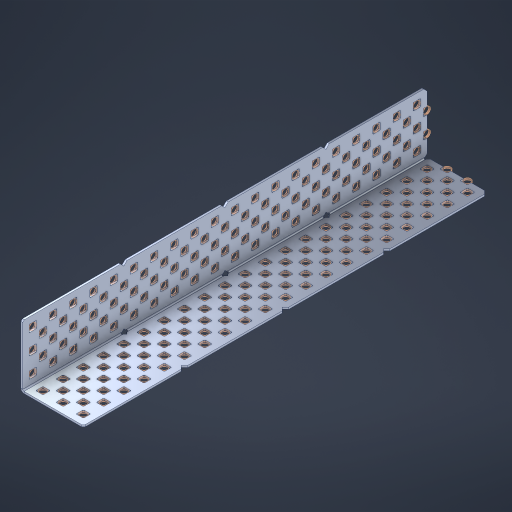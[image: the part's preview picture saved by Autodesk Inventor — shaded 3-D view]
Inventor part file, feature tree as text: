
AUTODESK INVENTOR PART (.ipt)
format: ipt  version: 2023 (Build 270158000, 158)  size: 2,148,352 bytes
history: native  units: in
note: dims shown in document units (in); Inventor stores cm internally (conversion verified against a paired STEP export)
features: other x206, extrude x198, sheet_metal_op x8, sketch x7, pattern_linear x3, mirror x1, chamfer x1
ambient origin geometry x8: Origin, YZ Plane, XZ Plane, XY Plane, X Axis, Y Axis, Z Axis, Center Point
bodies: Solid1 (feature_tree), Body (feature_tree)
feature tree (424):
  sheet_metal_op  "Flanges"
  sheet_metal_op  "Body Pattern"
  pattern_linear  "Center Double"  Spacing1=1.5in  [1 undecoded]
  pattern_linear  "Center Pattern"  Spacing1=0.1875in  [1 undecoded]
  other  "Arc Length"
  pattern_linear  "Notch Pattern"  Spacing1=0.0469in  [1 undecoded]
  other  "Diagonal Plane"
  mirror  "Everything Mirrored"
  chamfer  "End Chamfer"
  sketch  "Sketch1"  dims[d0=1.5in]
  other  "Plate1"
  sketch  "Sketch2"  dims[d1=10.0in]
  other  "Plate2"
  sheet_metal_op  "Bend1"
  sheet_metal_op  "Corner1"
  sketch  "Sketch8"  dims[d2=0.0469in]
  sketch  "Sketch9"  dims[d3=0.0469in]
  other  "Srf91"
  sheet_metal_op  "Body Pattern Sketch"
  other  "Srf92"
  sketch  "Sketch13"  dims[d4=0.0234in]
  sketch  "Sketch15"  dims[d5=0.0938in]
  sketch  "Sketch16"  dims[d6=0.0469in d7=1.5in d8=90.0deg d9=0.0312in d10=0.1875in d11=0.0469in d12=0.0469in d49=0.182in d50=0.02in d52=0.25in d53=0.0469in d54=0.0in d55=0.172in d56=1.0in d57=0.0in d85=0.1473in d86=0.1659in d89=0.0469in d90=0.0in d91=0.04in d92=0.0491in d95=2.5in d96=0.04in d97=0.25in d98=45.0deg d106=0.182in d107=0.02in d110=0.0469in d111=0.0in d112=0.172in d113=0.5in d114=0.0in d117=0.5in d126=0.0491in d127=0.1227in d128=0.08in d129=0.04in d130=2.5in d131=0.25in d132=7.874in d134=0.5in d135=1.1811in d137=0.5in d140=0.5in d141=1.0in d142=0.3937in d144=0.5in d145=0.071in d146=0.7874in d148=0.5in]
  other  "Srf786"
  other  "Srf856"
  other  "Srf889"
  other  "Srf890"
  other  "Srf891"
  other  "Srf1275"
  other  "Srf1276"
  other  "Srf1278"
  other  "Srf1277"
  other  "Srf1285"
  other  "Srf1286"
  other  "Srf1287"
  other  "Srf1445"
  other  "Srf1446"
  other  "Srf1447"
  other  "Srf1448"
  other  "Srf1449"
  other  "Srf1537"
  other  "Srf1538"
  other  "Srf1539"
  other  "Srf1540"
  other  "Srf1541"
  other  "Srf1807"
  other  "Srf1808"
  other  "Srf1809"
  other  "Srf1810"
  other  "Srf1811"
  other  "Srf1812"
  other  "Srf1813"
  other  "Srf1814"
  other  "Srf1815"
  other  "Srf1816"
  other  "Srf1817"
  other  "Srf1959"
  other  "Srf1960"
  other  "Srf1961"
  other  "Srf1962"
  other  "Srf1963"
  other  "Srf1964"
  other  "Srf1965"
  other  "Srf1966"
  other  "Srf1967"
  other  "Srf1968"
  other  "Srf1969"
  other  "Srf2009"
  other  "Srf2010"
  other  "Srf2011"
  other  "Srf2012"
  other  "Srf2013"
  other  "Srf2014"
  other  "Srf2015"
  other  "Srf2016"
  other  "Srf2017"
  other  "Srf2018"
  other  "Srf2019"
  other  "Srf2020"
  other  "Srf2021"
  other  "Srf2022"
  other  "Srf2023"
  other  "Srf2024"
  other  "Srf2025"
  other  "Srf2026"
  other  "Srf2027"
  other  "Srf2028"
  other  "Srf2043"
  other  "Srf2044"
  other  "Srf2045"
  other  "Srf2046"
  other  "Srf2047"
  other  "Srf2048"
  other  "Srf2049"
  other  "Srf2050"
  other  "Srf2051"
  other  "Srf2052"
  other  "Srf2053"
  other  "Srf2054"
  other  "Srf2055"
  other  "Srf2056"
  other  "Srf2057"
  other  "Srf2058"
  other  "Srf2059"
  other  "Srf2060"
  other  "Srf2061"
  other  "Srf2076"
  other  "Srf2077"
  other  "Srf2078"
  other  "Srf2079"
  other  "Srf2080"
  other  "Srf2081"
  other  "Srf2082"
  other  "Srf2083"
  other  "Srf2084"
  other  "Srf2085"
  other  "Srf2086"
  other  "Srf2087"
  other  "Srf2088"
  other  "Srf2089"
  other  "Srf2090"
  other  "Srf2091"
  other  "Srf2092"
  other  "Srf2093"
  other  "Srf2094"
  other  "Srf2095"
  other  "Srf2096"
  other  "Srf2097"
  other  "Srf2098"
  other  "Srf2099"
  other  "Srf2100"
  other  "Srf2101"
  other  "Srf2102"
  other  "Srf2103"
  other  "Srf2104"
  other  "Srf2105"
  other  "Srf2106"
  other  "Srf2107"
  other  "Srf2108"
  other  "Srf2109"
  other  "Srf2110"
  other  "Srf2111"
  other  "Srf2112"
  other  "Srf2113"
  other  "Srf2114"
  other  "Srf2115"
  other  "Srf2116"
  other  "Srf2117"
  other  "Srf2118"
  other  "Srf2119"
  other  "Srf2120"
  other  "Srf2121"
  other  "Srf2122"
  other  "Srf2123"
  other  "Srf2124"
  other  "Srf2125"
  other  "Srf2126"
  other  "Srf2127"
  other  "Srf2128"
  other  "Srf2129"
  other  "Srf2130"
  other  "Srf2131"
  other  "Srf2132"
  other  "Srf2133"
  other  "Srf2179"
  other  "Srf2180"
  other  "Srf2181"
  other  "Srf2182"
  other  "Srf2183"
  other  "Srf2184"
  other  "Srf2185"
  other  "Srf2186"
  other  "Srf2187"
  other  "Srf2188"
  other  "Srf2189"
  other  "Srf2190"
  other  "Srf2191"
  other  "Srf2192"
  other  "Srf2193"
  other  "Srf2194"
  other  "Srf2195"
  other  "Srf2196"
  other  "Srf2197"
  other  "Srf2198"
  other  "Srf2199"
  other  "Srf2200"
  other  "Srf2201"
  other  "Srf2202"
  other  "Srf2203"
  other  "Srf2204"
  other  "Srf2205"
  other  "Srf2206"
  other  "Srf2207"
  other  "Srf2208"
  other  "Srf2209"
  other  "Srf2210"
  other  "Srf2211"
  other  "Srf2212"
  other  "Srf2213"
  other  "Srf2214"
  other  "Srf2215"
  other  "Srf2216"
  other  "Srf2217"
  other  "Srf2218"
  other  "Srf2219"
  other  "Srf2220"
  other  "Srf2221"
  other  "Srf2222"
  other  "Srf2223"
  other  "Srf2224"
  other  "Srf2225"
  other  "Srf2226"
  other  "Srf2227"
  other  "Srf2228"
  other  "Srf2229"
  other  "Srf2230"
  other  "Srf2231"
  other  "Srf2232"
  other  "Srf2233"
  other  "Srf2234"
  other  "Srf2235"
  sheet_metal_op  "Body Stamp"
  sheet_metal_op  "Body Circle"
  other  "Center Stamp"
  other  "Center Circle"
  sheet_metal_op  "Notch"
  extrude  "ExtrusionSrf92"  Depth=0.0469in
  extrude  "ExtrusionSrf856"  Depth=0.3937in
  extrude  "ExtrusionSrf889"  Depth=0.02in
  extrude  "ExtrusionSrf890"  Depth=0.25in
  extrude  "ExtrusionSrf891"  Depth=0.0469in
  extrude  "ExtrusionSrf1275"  TaperAngle=0.0deg  [1 undecoded]
  extrude  "ExtrusionSrf1276"  Depth=0.3937in
  extrude  "ExtrusionSrf1277"  Depth=0.3937in TaperAngle=0.0deg
  extrude  "ExtrusionSrf1345"  Depth=0.3937in
  extrude  "ExtrusionSrf1346"  Depth=0.3937in
  extrude  "ExtrusionSrf1347"  Depth=0.0469in
  extrude  "ExtrusionSrf1348"  Depth=0.3937in TaperAngle=0.0deg
  extrude  "ExtrusionSrf1445"  Depth=0.3937in
  extrude  "ExtrusionSrf1446"  Depth=0.25in TaperAngle=45.0deg
  extrude  "ExtrusionSrf1447"  Depth=0.3937in
  extrude  "ExtrusionSrf1448"  Depth=0.02in
  extrude  "ExtrusionSrf1449"  Depth=0.0469in
  extrude  "ExtrusionSrf1537"  TaperAngle=0.0deg  [1 undecoded]
  extrude  "ExtrusionSrf1538"  Depth=0.3937in
  extrude  "ExtrusionSrf1539"  Depth=0.3937in TaperAngle=0.0deg
  extrude  "ExtrusionSrf1540"  Depth=0.3937in
  extrude  "ExtrusionSrf1541"  Depth=0.3937in
  extrude  "ExtrusionSrf1807"  Depth=0.3937in
  extrude  "ExtrusionSrf1808"  Depth=0.3937in
  extrude  "ExtrusionSrf1809"  Depth=0.3937in
  extrude  "ExtrusionSrf1810"  Depth=0.3937in
  extrude  "ExtrusionSrf1811"  Depth=0.25in
  extrude  "ExtrusionSrf1812"  Depth=0.3937in
  extrude  "ExtrusionSrf1813"  Depth=0.3937in
  extrude  "ExtrusionSrf1814"  Depth=0.3937in
  extrude  "ExtrusionSrf1815"  Depth=0.3937in
  extrude  "ExtrusionSrf1816"  Depth=0.3937in
  extrude  "ExtrusionSrf1817"  Depth=0.3937in
  extrude  "ExtrusionSrf1959"  Depth=0.3937in
  extrude  "ExtrusionSrf1960"  [1 undecoded]
  extrude  "ExtrusionSrf1961"  [1 undecoded]
  extrude  "ExtrusionSrf1962"  [1 undecoded]
  extrude  "ExtrusionSrf1963"  [1 undecoded]
  extrude  "ExtrusionSrf1964"  [1 undecoded]
  extrude  "ExtrusionSrf1965"  [1 undecoded]
  extrude  "ExtrusionSrf1966"  [1 undecoded]
  extrude  "ExtrusionSrf1967"  [1 undecoded]
  extrude  "ExtrusionSrf1968"  [1 undecoded]
  extrude  "ExtrusionSrf1969"  [1 undecoded]
  extrude  "ExtrusionSrf2009"  [1 undecoded]
  extrude  "ExtrusionSrf2010"  [1 undecoded]
  extrude  "ExtrusionSrf2011"  [1 undecoded]
  extrude  "ExtrusionSrf2012"  [1 undecoded]
  extrude  "ExtrusionSrf2013"  [1 undecoded]
  extrude  "ExtrusionSrf2014"  [1 undecoded]
  extrude  "ExtrusionSrf2015"  [1 undecoded]
  extrude  "ExtrusionSrf2016"  [1 undecoded]
  extrude  "ExtrusionSrf2017"  [1 undecoded]
  extrude  "ExtrusionSrf2018"  [1 undecoded]
  extrude  "ExtrusionSrf2019"  [1 undecoded]
  extrude  "ExtrusionSrf2020"  [1 undecoded]
  extrude  "ExtrusionSrf2021"  [1 undecoded]
  extrude  "ExtrusionSrf2022"  [1 undecoded]
  extrude  "ExtrusionSrf2023"  [1 undecoded]
  extrude  "ExtrusionSrf2024"  [1 undecoded]
  extrude  "ExtrusionSrf2025"  [1 undecoded]
  extrude  "ExtrusionSrf2026"  [1 undecoded]
  extrude  "ExtrusionSrf2027"  [1 undecoded]
  extrude  "ExtrusionSrf2028"  [1 undecoded]
  extrude  "ExtrusionSrf2043"  [1 undecoded]
  extrude  "ExtrusionSrf2044"  [1 undecoded]
  extrude  "ExtrusionSrf2045"  [1 undecoded]
  extrude  "ExtrusionSrf2046"  [1 undecoded]
  extrude  "ExtrusionSrf2047"  [1 undecoded]
  extrude  "ExtrusionSrf2048"  [1 undecoded]
  extrude  "ExtrusionSrf2049"  [1 undecoded]
  extrude  "ExtrusionSrf2050"  [1 undecoded]
  extrude  "ExtrusionSrf2051"  [1 undecoded]
  extrude  "ExtrusionSrf2052"  [1 undecoded]
  extrude  "ExtrusionSrf2053"  [1 undecoded]
  extrude  "ExtrusionSrf2054"  [1 undecoded]
  extrude  "ExtrusionSrf2055"  [1 undecoded]
  extrude  "ExtrusionSrf2056"  [1 undecoded]
  extrude  "ExtrusionSrf2057"  [1 undecoded]
  extrude  "ExtrusionSrf2058"  [1 undecoded]
  extrude  "ExtrusionSrf2059"  [1 undecoded]
  extrude  "ExtrusionSrf2060"  [1 undecoded]
  extrude  "ExtrusionSrf2061"  [1 undecoded]
  extrude  "ExtrusionSrf2076"  [1 undecoded]
  extrude  "ExtrusionSrf2077"  [1 undecoded]
  extrude  "ExtrusionSrf2078"  [1 undecoded]
  extrude  "ExtrusionSrf2079"  [1 undecoded]
  extrude  "ExtrusionSrf2080"  [1 undecoded]
  extrude  "ExtrusionSrf2081"  [1 undecoded]
  extrude  "ExtrusionSrf2082"  [1 undecoded]
  extrude  "ExtrusionSrf2083"  [1 undecoded]
  extrude  "ExtrusionSrf2084"  [1 undecoded]
  extrude  "ExtrusionSrf2085"  [1 undecoded]
  extrude  "ExtrusionSrf2086"  [1 undecoded]
  extrude  "ExtrusionSrf2087"  [1 undecoded]
  extrude  "ExtrusionSrf2088"  [1 undecoded]
  extrude  "ExtrusionSrf2089"  [1 undecoded]
  extrude  "ExtrusionSrf2090"  [1 undecoded]
  extrude  "ExtrusionSrf2091"  [1 undecoded]
  extrude  "ExtrusionSrf2092"  [1 undecoded]
  extrude  "ExtrusionSrf2093"  [1 undecoded]
  extrude  "ExtrusionSrf2094"  [1 undecoded]
  extrude  "ExtrusionSrf2095"  [1 undecoded]
  extrude  "ExtrusionSrf2096"  [1 undecoded]
  extrude  "ExtrusionSrf2097"  [1 undecoded]
  extrude  "ExtrusionSrf2098"  [1 undecoded]
  extrude  "ExtrusionSrf2099"  [1 undecoded]
  extrude  "ExtrusionSrf2100"  [1 undecoded]
  extrude  "ExtrusionSrf2101"  [1 undecoded]
  extrude  "ExtrusionSrf2102"  [1 undecoded]
  extrude  "ExtrusionSrf2103"  [1 undecoded]
  extrude  "ExtrusionSrf2104"  [1 undecoded]
  extrude  "ExtrusionSrf2105"  [1 undecoded]
  extrude  "ExtrusionSrf2106"  [1 undecoded]
  extrude  "ExtrusionSrf2107"  [1 undecoded]
  extrude  "ExtrusionSrf2108"  [1 undecoded]
  extrude  "ExtrusionSrf2109"  [1 undecoded]
  extrude  "ExtrusionSrf2110"  [1 undecoded]
  extrude  "ExtrusionSrf2111"  [1 undecoded]
  extrude  "ExtrusionSrf2112"  [1 undecoded]
  extrude  "ExtrusionSrf2113"  [1 undecoded]
  extrude  "ExtrusionSrf2114"  [1 undecoded]
  extrude  "ExtrusionSrf2115"  [1 undecoded]
  extrude  "ExtrusionSrf2116"  [1 undecoded]
  extrude  "ExtrusionSrf2117"  [1 undecoded]
  extrude  "ExtrusionSrf2118"  [1 undecoded]
  extrude  "ExtrusionSrf2119"  [1 undecoded]
  extrude  "ExtrusionSrf2120"  [1 undecoded]
  extrude  "ExtrusionSrf2121"  [1 undecoded]
  extrude  "ExtrusionSrf2122"  [1 undecoded]
  extrude  "ExtrusionSrf2123"  [1 undecoded]
  extrude  "ExtrusionSrf2124"  [1 undecoded]
  extrude  "ExtrusionSrf2125"  [1 undecoded]
  extrude  "ExtrusionSrf2126"  [1 undecoded]
  extrude  "ExtrusionSrf2127"  [1 undecoded]
  extrude  "ExtrusionSrf2128"  [1 undecoded]
  extrude  "ExtrusionSrf2129"  [1 undecoded]
  extrude  "ExtrusionSrf2130"  [1 undecoded]
  extrude  "ExtrusionSrf2131"  [1 undecoded]
  extrude  "ExtrusionSrf2132"  [1 undecoded]
  extrude  "ExtrusionSrf2133"  [1 undecoded]
  extrude  "ExtrusionSrf2179"  [1 undecoded]
  extrude  "ExtrusionSrf2180"  [1 undecoded]
  extrude  "ExtrusionSrf2181"  [1 undecoded]
  extrude  "ExtrusionSrf2182"  [1 undecoded]
  extrude  "ExtrusionSrf2183"  [1 undecoded]
  extrude  "ExtrusionSrf2184"  [1 undecoded]
  extrude  "ExtrusionSrf2185"  [1 undecoded]
  extrude  "ExtrusionSrf2186"  [1 undecoded]
  extrude  "ExtrusionSrf2187"  [1 undecoded]
  extrude  "ExtrusionSrf2188"  [1 undecoded]
  extrude  "ExtrusionSrf2189"  [1 undecoded]
  extrude  "ExtrusionSrf2190"  [1 undecoded]
  extrude  "ExtrusionSrf2191"  [1 undecoded]
  extrude  "ExtrusionSrf2192"  [1 undecoded]
  extrude  "ExtrusionSrf2193"  [1 undecoded]
  extrude  "ExtrusionSrf2194"  [1 undecoded]
  extrude  "ExtrusionSrf2195"  [1 undecoded]
  extrude  "ExtrusionSrf2196"  [1 undecoded]
  extrude  "ExtrusionSrf2197"  [1 undecoded]
  extrude  "ExtrusionSrf2198"  [1 undecoded]
  extrude  "ExtrusionSrf2199"  [1 undecoded]
  extrude  "ExtrusionSrf2200"  [1 undecoded]
  extrude  "ExtrusionSrf2201"  [1 undecoded]
  extrude  "ExtrusionSrf2202"  [1 undecoded]
  extrude  "ExtrusionSrf2203"  [1 undecoded]
  extrude  "ExtrusionSrf2204"  [1 undecoded]
  extrude  "ExtrusionSrf2205"  [1 undecoded]
  extrude  "ExtrusionSrf2206"  [1 undecoded]
  extrude  "ExtrusionSrf2207"  [1 undecoded]
  extrude  "ExtrusionSrf2208"  [1 undecoded]
  extrude  "ExtrusionSrf2209"  [1 undecoded]
  extrude  "ExtrusionSrf2210"  [1 undecoded]
  extrude  "ExtrusionSrf2211"  [1 undecoded]
  extrude  "ExtrusionSrf2212"  [1 undecoded]
  extrude  "ExtrusionSrf2213"  [1 undecoded]
  extrude  "ExtrusionSrf2214"  [1 undecoded]
  extrude  "ExtrusionSrf2215"  [1 undecoded]
  extrude  "ExtrusionSrf2216"  [1 undecoded]
  extrude  "ExtrusionSrf2217"  [1 undecoded]
  extrude  "ExtrusionSrf2218"  [1 undecoded]
  extrude  "ExtrusionSrf2219"  [1 undecoded]
  extrude  "ExtrusionSrf2220"  [1 undecoded]
  extrude  "ExtrusionSrf2221"  [1 undecoded]
  extrude  "ExtrusionSrf2222"  [1 undecoded]
  extrude  "ExtrusionSrf2223"  [1 undecoded]
  extrude  "ExtrusionSrf2224"  [1 undecoded]
  extrude  "ExtrusionSrf2225"  [1 undecoded]
  extrude  "ExtrusionSrf2226"  [1 undecoded]
  extrude  "ExtrusionSrf2227"  [1 undecoded]
  extrude  "ExtrusionSrf2228"  [1 undecoded]
  extrude  "ExtrusionSrf2229"  [1 undecoded]
  extrude  "ExtrusionSrf2230"  [1 undecoded]
  extrude  "ExtrusionSrf2231"  [1 undecoded]
  extrude  "ExtrusionSrf2232"  [1 undecoded]
  extrude  "ExtrusionSrf2233"  [1 undecoded]
  extrude  "ExtrusionSrf2234"  [1 undecoded]
  extrude  "ExtrusionSrf2235"  [1 undecoded]
note: 169 required parameter values undecoded (feature->parameter linkage not recoverable at this tier; creation-order binding heuristic only, values carry confidence <= 0.55)
